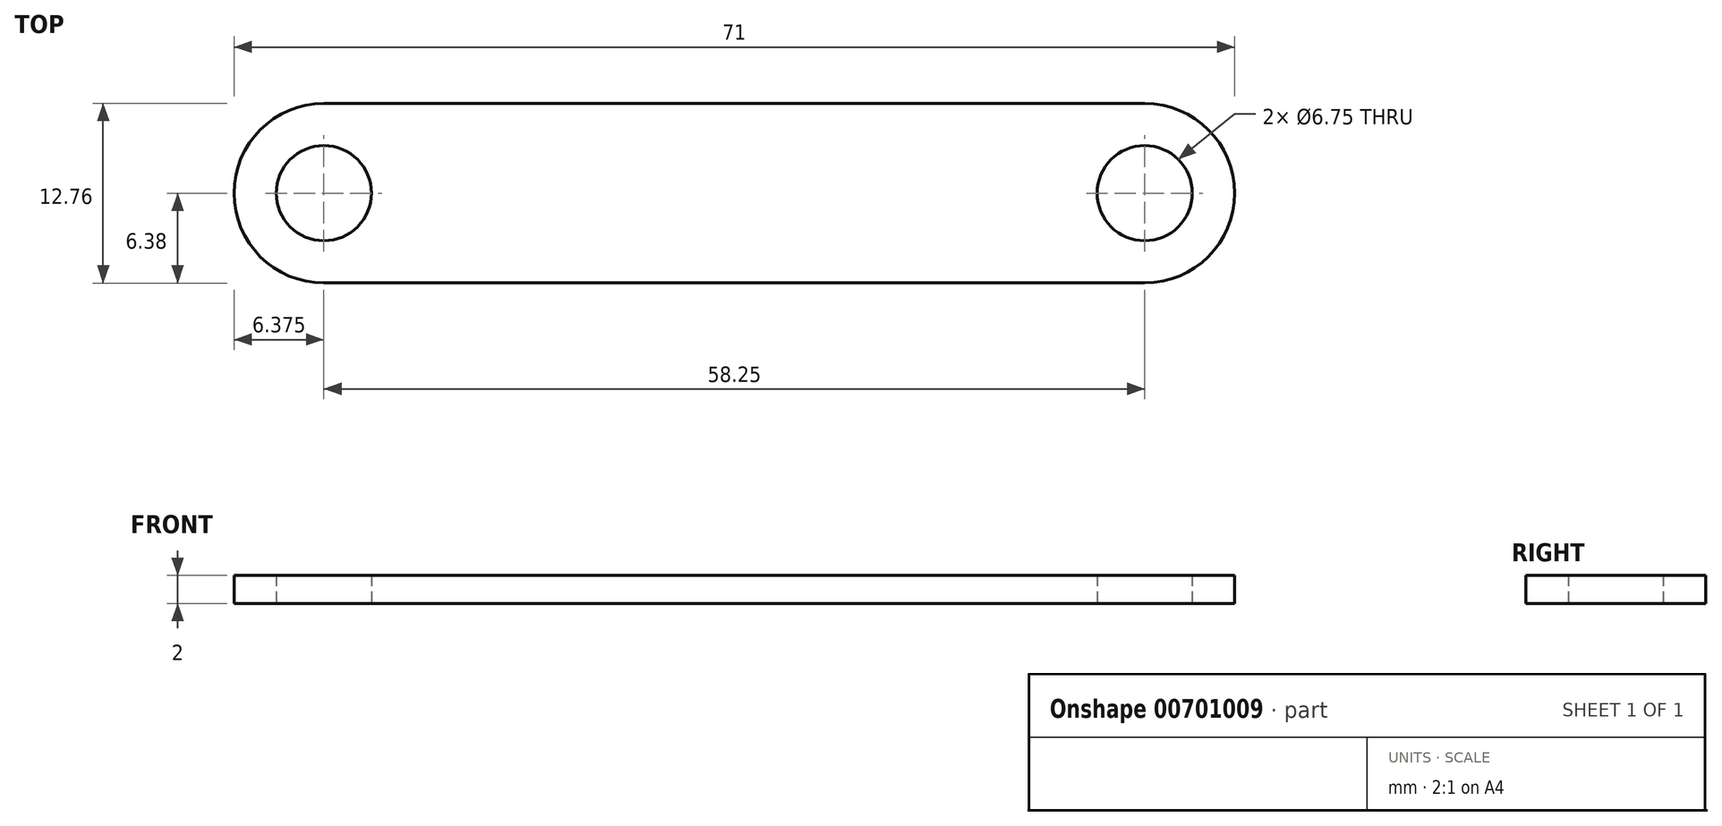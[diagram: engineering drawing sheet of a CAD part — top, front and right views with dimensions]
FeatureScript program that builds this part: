
annotation { "Feature Type Name" : "Feature", "Feature Type Description" : "" }
export const myFeature = defineFeature(function(context is Context, id is Id, definition is map)
    precondition{}
    {
        {
            var Q0;
            Q0=qCreatedBy(makeId("Top.planeOp"),FACE);
            var sketch = newSketch(context, id + "F0", { "sketchPlane" : qUnion([Q0])});
            skPoint(sketch, "E0.middle", {"position": v(0, 0) * mm});
            skLineSegment(sketch, "E1", {"start": v(-32.5, 0) * mm, "end": v(32.5, 0) * mm, "construction": true});
            skCircle(sketch, "E2", {"center": v(-29.12, 0) * mm, "radius": 3.38 * mm});
            skLineSegment(sketch, "E3", {"start": v(-32.5, 0) * mm, "end": v(-29.12, 0) * mm, "construction": true});
            skLineSegment(sketch, "E4.0", {"start": v(-29.12, -6.38) * mm, "end": v(29.12, -6.38) * mm});
            skArc(sketch, "E5.0", {"start": v(-29.12, 6.38) * mm, "mid": v(-35.5, 0) * mm, "end": v(-29.12, -6.38) * mm});
            skLineSegment(sketch, "E6", {"start": v(0, 0) * mm, "end": v(0, 16.84) * mm, "construction": true});
            skCircle(sketch, "E7.MirrorC", {"center": v(29.12, 0) * mm, "radius": 3.38 * mm});
            skArc(sketch, "E8.MirrorC", {"start": v(29.12, 6.38) * mm, "mid": v(35.5, 0) * mm, "end": v(29.12, -6.38) * mm});
            skLineSegment(sketch, "E9.MirrorCS", {"start": v(-29.12, 6.38) * mm, "end": v(29.12, 6.38) * mm});
            skPoint(sketch, "E10.orphan", {"position": v(32.5, 6.38) * mm});
            skPoint(sketch, "E11.orphan", {"position": v(32.5, -6.38) * mm});
            skPoint(sketch, "E12.orphan", {"position": v(-32.5, -6.38) * mm});
            skPoint(sketch, "E13.orphan", {"position": v(-32.5, 6.38) * mm});
            skSolve(sketch);
        }
        {
            var Q0;
            Q0=makeQuery(id+"F0.imprint","IMPRINT",FACE,{"disambiguationData":[TD([[makeQuery(id+"F0.imprint","IMPRINT",EDGE,{"derivedFrom":sQuery(id+"F0.wireOp",EDGE,"E2")}),-1.0]])]});
            extrude(context, id + "F1", {"entities" : qUnion([Q0]), "depth" : 2 * mm, "offsetDistance" : 25 * mm});
        }
    });
